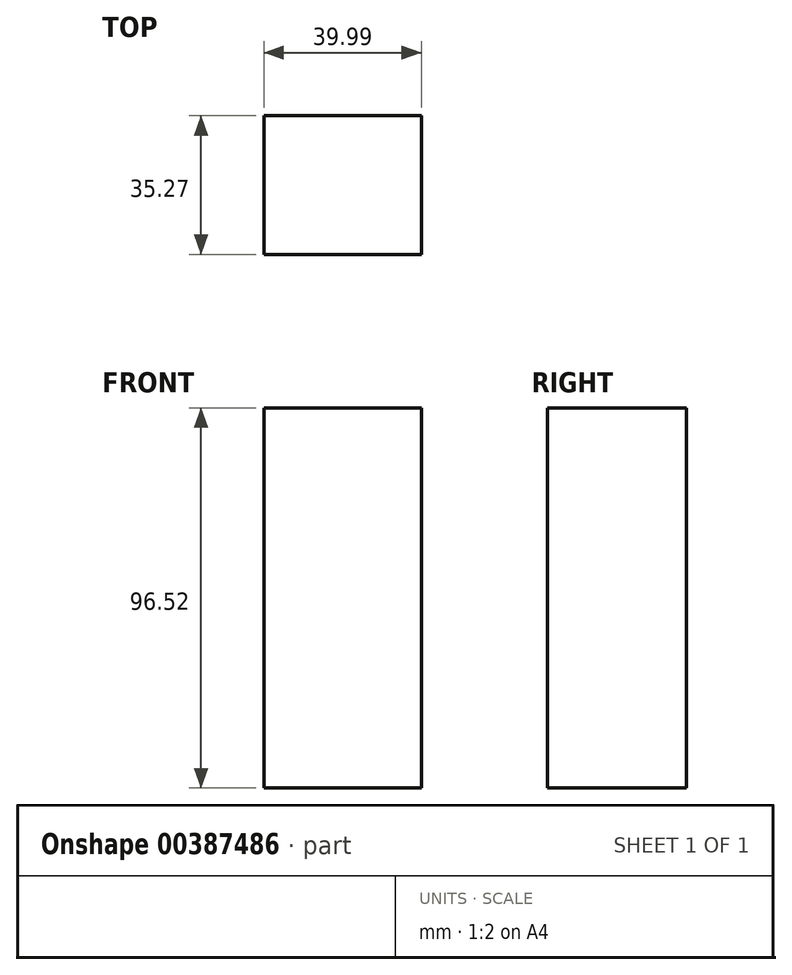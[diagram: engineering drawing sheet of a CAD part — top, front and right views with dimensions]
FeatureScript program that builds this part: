
annotation { "Feature Type Name" : "Feature", "Feature Type Description" : "" }
export const myFeature = defineFeature(function(context is Context, id is Id, definition is map)
    precondition{}
    {
        {
            var Q0;
            Q0=qCreatedBy(makeId("Top.planeOp"),FACE);
            var sketch = newSketch(context, id + "F0", { "sketchPlane" : qUnion([Q0])});
            skLineSegment(sketch, "E0.bottom", {"start": v(-56.18, 6.56) * mm, "end": v(-16.19, 6.56) * mm});
            skLineSegment(sketch, "E0.top", {"start": v(-56.18, -28.7) * mm, "end": v(-16.19, -28.7) * mm});
            skLineSegment(sketch, "E0.left", {"start": v(-56.18, 6.56) * mm, "end": v(-56.18, -28.7) * mm});
            skLineSegment(sketch, "E0.right", {"start": v(-16.19, 6.56) * mm, "end": v(-16.19, -28.7) * mm});
            skSolve(sketch);
        }
        {
            var Q0;
            Q0 = qSketchRegion(id + "F0", true);
            extrude(context, id + "F1", {"entities" : qUnion([Q0]), "depth" : 96.52 * mm});
        }
    });
